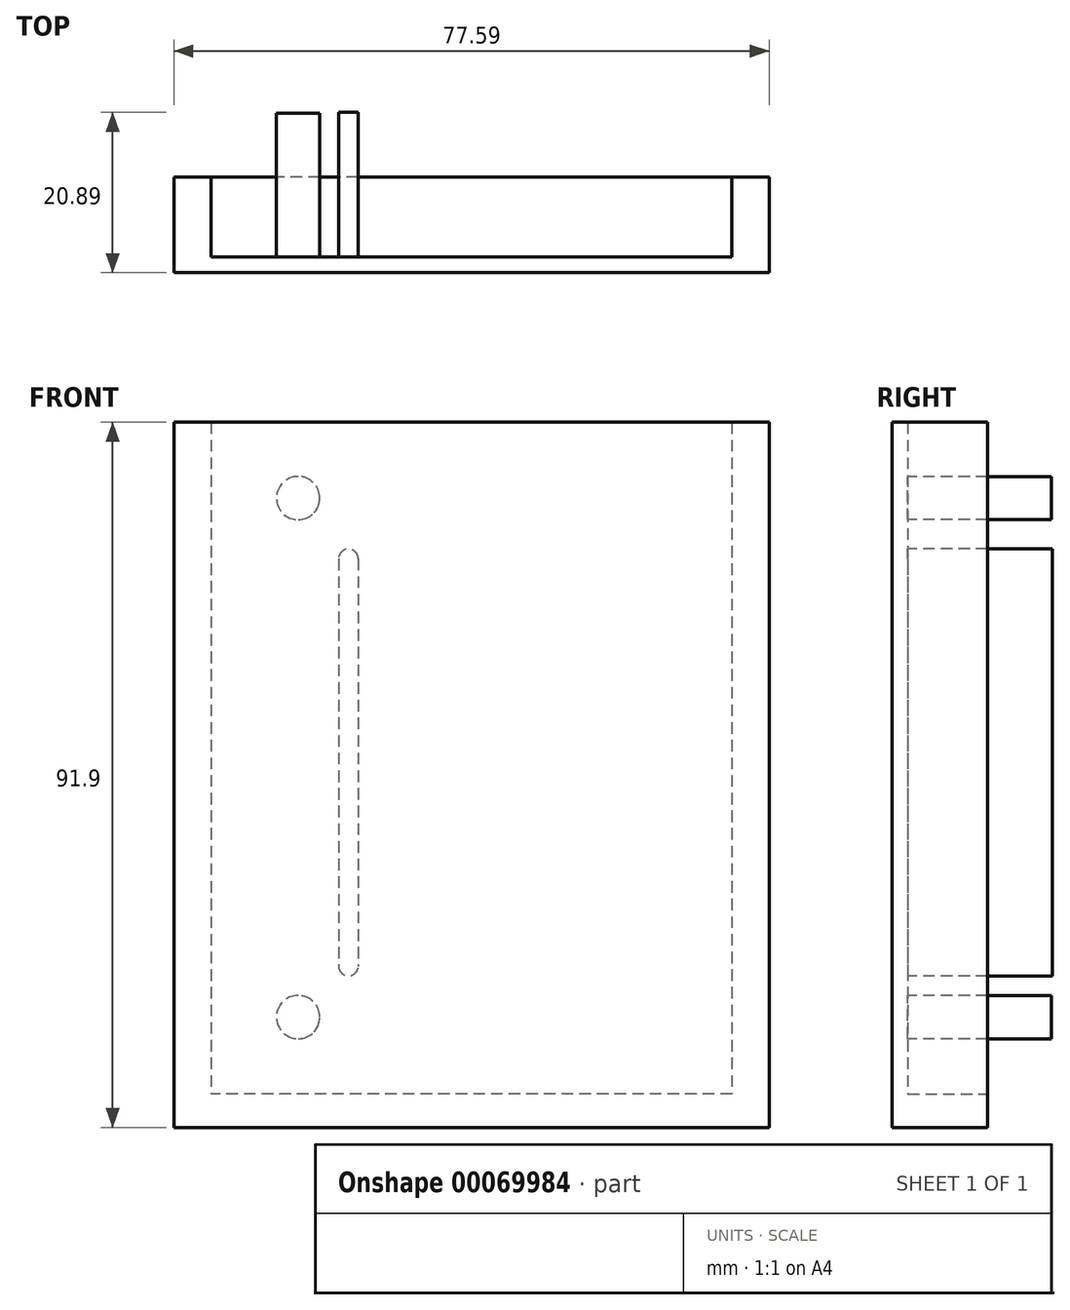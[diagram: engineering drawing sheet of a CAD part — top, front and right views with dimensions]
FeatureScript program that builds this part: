
annotation { "Feature Type Name" : "Feature", "Feature Type Description" : "" }
export const myFeature = defineFeature(function(context is Context, id is Id, definition is map)
    precondition{}
    {
        {
            var Q0;
            Q0=qCreatedBy(makeId("Front.planeOp"),FACE);
            var sketch = newSketch(context, id + "F0", { "sketchPlane" : qUnion([Q0])});
            skLineSegment(sketch, "E0.bottom", {"start": v(-37.64, 42.14) * mm, "end": v(39.95, 42.14) * mm});
            skLineSegment(sketch, "E0.top", {"start": v(-37.64, -49.76) * mm, "end": v(39.95, -49.76) * mm});
            skLineSegment(sketch, "E0.left", {"start": v(-37.64, 42.14) * mm, "end": v(-37.64, -49.76) * mm});
            skLineSegment(sketch, "E0.right", {"start": v(39.95, 42.14) * mm, "end": v(39.95, -49.76) * mm});
            skSolve(sketch);
        }
        {
            var Q0;
            Q0=makeQuery(id+"F0.imprint","IMPRINT",FACE,{"disambiguationData":[TD([[makeQuery(id+"F0.imprint","IMPRINT",EDGE,{"derivedFrom":sQuery(id+"F0.wireOp",EDGE,"E0.bottom")}),-1.0]])]});
            extrude(context, id + "F1", {"entities" : qUnion([Q0]), "depth" : 12.47 * mm});
        }
        {
            var Q0;
            Q0=qCreatedBy(makeId("Front.planeOp"),FACE);
            var sketch = newSketch(context, id + "F2", { "sketchPlane" : qUnion([Q0])});
            skLineSegment(sketch, "E1.bottom", {"start": v(35.1, 46.07) * mm, "end": v(-32.79, 46.07) * mm});
            skLineSegment(sketch, "E1.top", {"start": v(35.1, -45.37) * mm, "end": v(-32.79, -45.37) * mm});
            skLineSegment(sketch, "E1.left", {"start": v(35.1, 46.07) * mm, "end": v(35.1, -45.37) * mm});
            skLineSegment(sketch, "E1.right", {"start": v(-32.79, 46.07) * mm, "end": v(-32.79, -45.37) * mm});
            skSolve(sketch);
        }
        {
            var Q0;
            Q0 = qSketchRegion(id + "F2", true);
            extrude(context, id + "F3", {"entities" : qUnion([Q0]), "operationType" : NewBodyOperationType.REMOVE, "depth" : 10.4 * mm});
        }
        {
            var Q0;
            Q0=makeQuery(id+"F3.boolean.opBoolean","COPY",FACE,{"derivedFrom":makeQuery(id+"F3.opExtrude","CAP_FACE",FACE,{"disambiguationData":[OSD([sQuery(id+"F2.wireOp",EDGE,"E1.bottom"),sQuery(id+"F2.wireOp",EDGE,"E1.top"),sQuery(id+"F2.wireOp",EDGE,"E1.left"),sQuery(id+"F2.wireOp",EDGE,"E1.right")])],"isStart":false})});
            var sketch = newSketch(context, id + "F4", { "sketchPlane" : qUnion([Q0])});
            skCircle(sketch, "E2", {"center": v(21.45, 32.26) * mm, "radius": 2.82 * mm});
            skCircle(sketch, "E3", {"center": v(21.45, -35.4) * mm, "radius": 2.82 * mm});
            skSolve(sketch);
        }
        {
            var Q0;
            Q0 = qSketchRegion(id + "F4", true);
            extrude(context, id + "F5", {"entities" : qUnion([Q0]), "operationType" : NewBodyOperationType.ADD, "depth" : 18.68 * mm});
        }
        {
            var Q0;
            Q0=makeQuery(id+"F3.boolean.opBoolean","COPY",FACE,{"derivedFrom":makeQuery(id+"F3.opExtrude","CAP_FACE",FACE,{"disambiguationData":[OSD([sQuery(id+"F2.wireOp",EDGE,"E1.bottom"),sQuery(id+"F2.wireOp",EDGE,"E1.top"),sQuery(id+"F2.wireOp",EDGE,"E1.left"),sQuery(id+"F2.wireOp",EDGE,"E1.right")])],"isStart":false})});
            var sketch = newSketch(context, id + "F6", { "sketchPlane" : qUnion([Q0])});
            skLineSegment(sketch, "E4", {"start": v(13.62, 24.36) * mm, "end": v(13.62, -28.75) * mm});
            skLineSegment(sketch, "E5", {"start": v(16.16, 24.36) * mm, "end": v(16.16, -28.75) * mm});
            skArc(sketch, "E6", {"start": v(16.16, 24.36) * mm, "mid": v(14.9, 25.63) * mm, "end": v(13.62, 24.36) * mm});
            skArc(sketch, "E7", {"start": v(13.62, -28.75) * mm, "mid": v(14.9, -30.02) * mm, "end": v(16.16, -28.75) * mm});
            skSolve(sketch);
        }
        {
            var Q0;
            Q0 = qSketchRegion(id + "F6", true);
            extrude(context, id + "F7", {"entities" : qUnion([Q0]), "operationType" : NewBodyOperationType.ADD, "depth" : 18.8 * mm});
        }
    });
